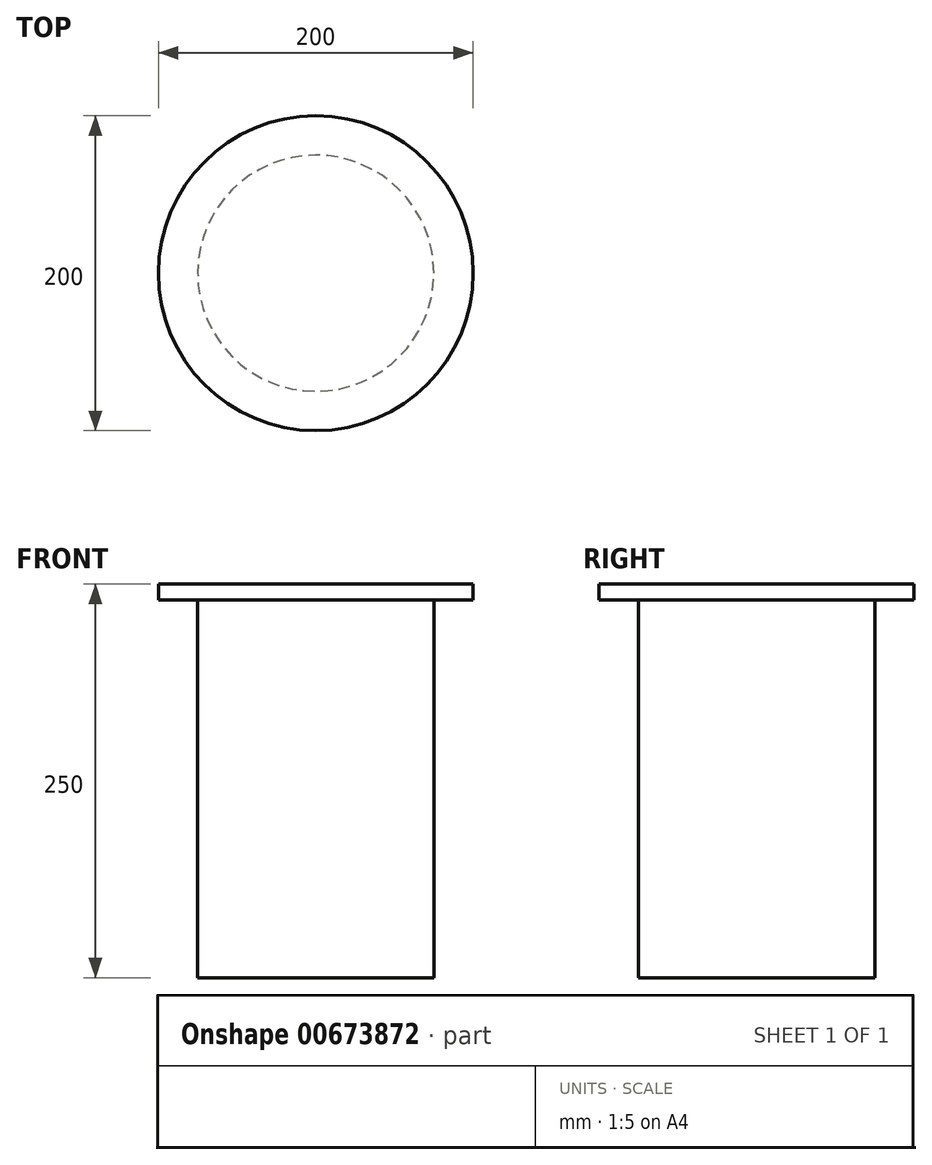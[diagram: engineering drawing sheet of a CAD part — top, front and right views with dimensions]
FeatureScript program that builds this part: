
annotation { "Feature Type Name" : "Feature", "Feature Type Description" : "" }
export const myFeature = defineFeature(function(context is Context, id is Id, definition is map)
    precondition{}
    {
        {
            var Q0;
            Q0=qCreatedBy(makeId("Top.planeOp"),FACE);
            var sketch = newSketch(context, id + "F0", { "sketchPlane" : qUnion([Q0])});
            skCircle(sketch, "E0", {"center": v(0, 0) * mm, "radius": 100 * mm});
            skCircle(sketch, "E1", {"center": v(0, 0) * mm, "radius": 75 * mm});
            skSolve(sketch);
        }
        {
            var Q0;
            Q0=makeQuery(id+"F0.imprint","IMPRINT",FACE,{"disambiguationData":[TD([[makeQuery(id+"F0.imprint","IMPRINT",EDGE,{"derivedFrom":sQuery(id+"F0.wireOp",EDGE,"E0")}),1.0]])]});
            var sketch = newSketch(context, id + "F1", { "sketchPlane" : qUnion([Q0])});
            skSolve(sketch);
        }
        {
            var Q0;
            Q0=makeQuery(id+"F1.imprint","IMPRINT",FACE,{"disambiguationData":[TD([[makeQuery(id+"F1.imprint","IMPRINT",EDGE,{"derivedFrom":makeQuery(id+"F0.imprint","IMPRINT",EDGE,{"derivedFrom":sQuery(id+"F0.wireOp",EDGE,"E0")})}),1.0]])]});
            extrude(context, id + "F2", {"entities" : qUnion([Q0]), "oppositeDirection" : true, "depth" : 10 * mm, "offsetDistance" : 25 * mm});
        }
        {
            var Q0;
            Q0=makeQuery(id+"F1.imprint","IMPRINT",FACE,{"disambiguationData":[TD([[makeQuery(id+"F1.imprint","IMPRINT",EDGE,{"derivedFrom":makeQuery(id+"F0.imprint","IMPRINT",EDGE,{"derivedFrom":sQuery(id+"F0.wireOp",EDGE,"E1")})}),1.0]])]});
            extrude(context, id + "F3", {"entities" : qUnion([Q0]), "operationType" : NewBodyOperationType.ADD, "oppositeDirection" : true, "depth" : 250 * mm, "offsetDistance" : 25 * mm});
        }
    });
